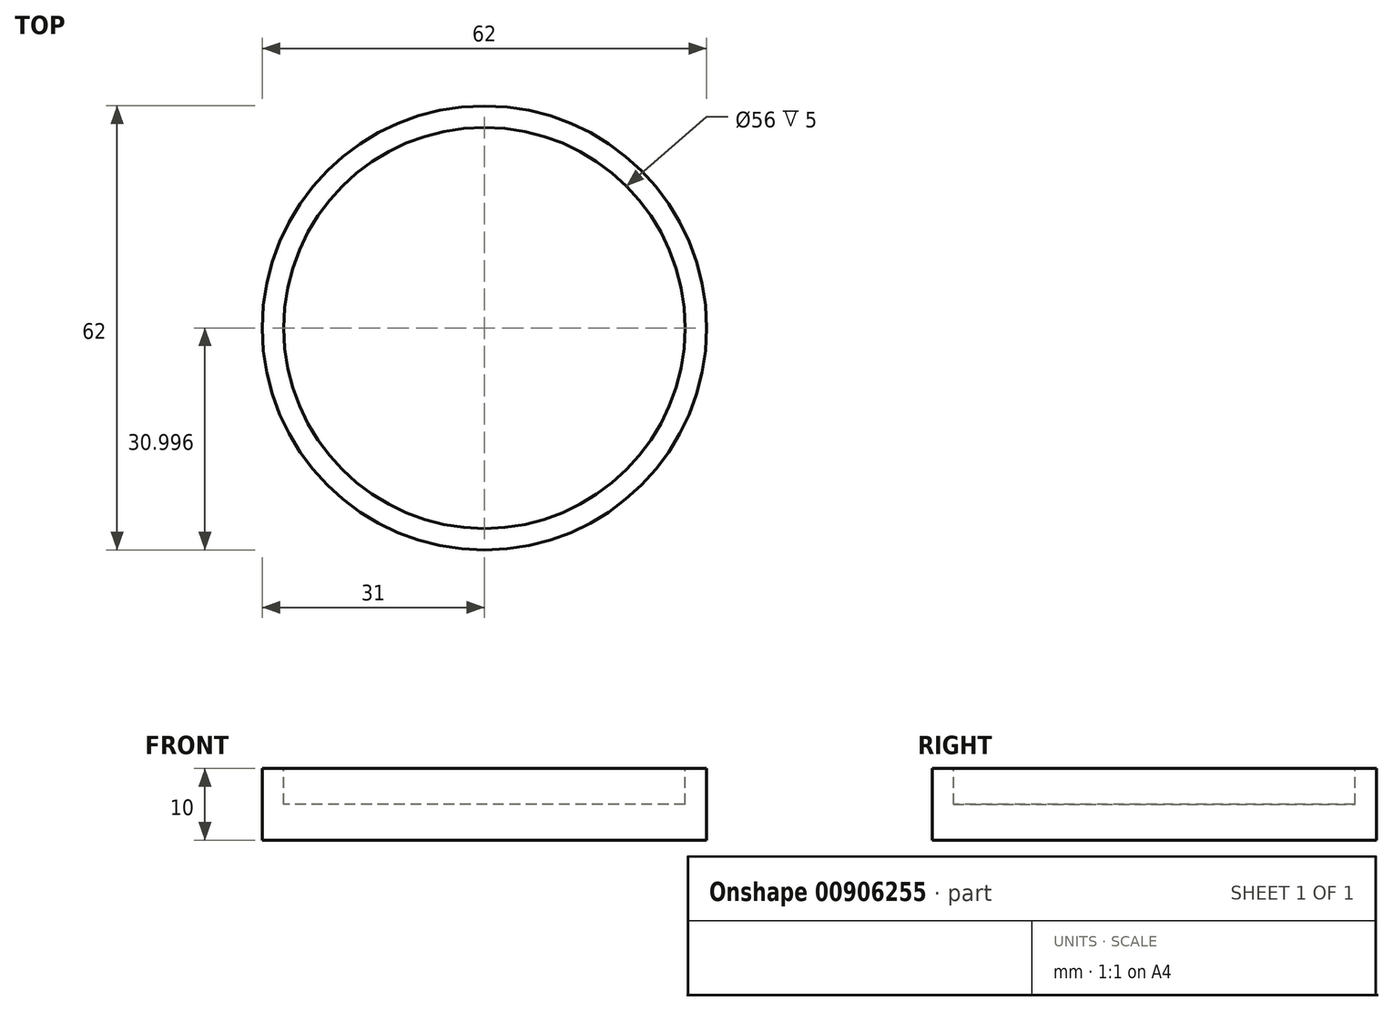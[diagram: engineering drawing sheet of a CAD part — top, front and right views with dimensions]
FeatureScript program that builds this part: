
annotation { "Feature Type Name" : "Feature", "Feature Type Description" : "" }
export const myFeature = defineFeature(function(context is Context, id is Id, definition is map)
    precondition{}
    {
        {
            var Q0;
            Q0=qCreatedBy(makeId("Top.planeOp"),FACE);
            var sketch = newSketch(context, id + "F0", { "sketchPlane" : qUnion([Q0])});
            skCircle(sketch, "E0", {"center": v(0, 1.29) * mm, "radius": 31 * mm});
            skSolve(sketch);
        }
        {
            var Q0;
            Q0=makeQuery(id+"F0.imprint","IMPRINT",FACE,{"disambiguationData":[TD([[makeQuery(id+"F0.imprint","IMPRINT",EDGE,{"derivedFrom":sQuery(id+"F0.wireOp",EDGE,"E0")}),1.0]])]});
            var Q1;
            Q1=sQuery(id+"F0.wireOp",EDGE,"E0");
            extrude(context, id + "F1", {"entities" : qUnion([Q0]), "surfaceEntities" : qUnion([Q1]), "depth" : 10 * mm, "offsetDistance" : 25.4 * mm});
        }
        {
            var Q0;
            Q0=makeQuery(id+"F1.opExtrude","CAP_FACE",FACE,{"disambiguationData":[OSD([sQuery(id+"F0.wireOp",EDGE,"E0")])],"isStart":false});
            var sketch = newSketch(context, id + "F2", { "sketchPlane" : qUnion([Q0])});
            skCircle(sketch, "E1", {"center": v(0, 1.29) * mm, "radius": 28 * mm});
            skSolve(sketch);
        }
        {
            var Q0;
            Q0 = qSketchRegion(id + "F2", true);
            extrude(context, id + "F3", {"entities" : qUnion([Q0]), "operationType" : NewBodyOperationType.REMOVE, "oppositeDirection" : true, "depth" : 5 * mm, "offsetDistance" : 25 * mm});
        }
    });
